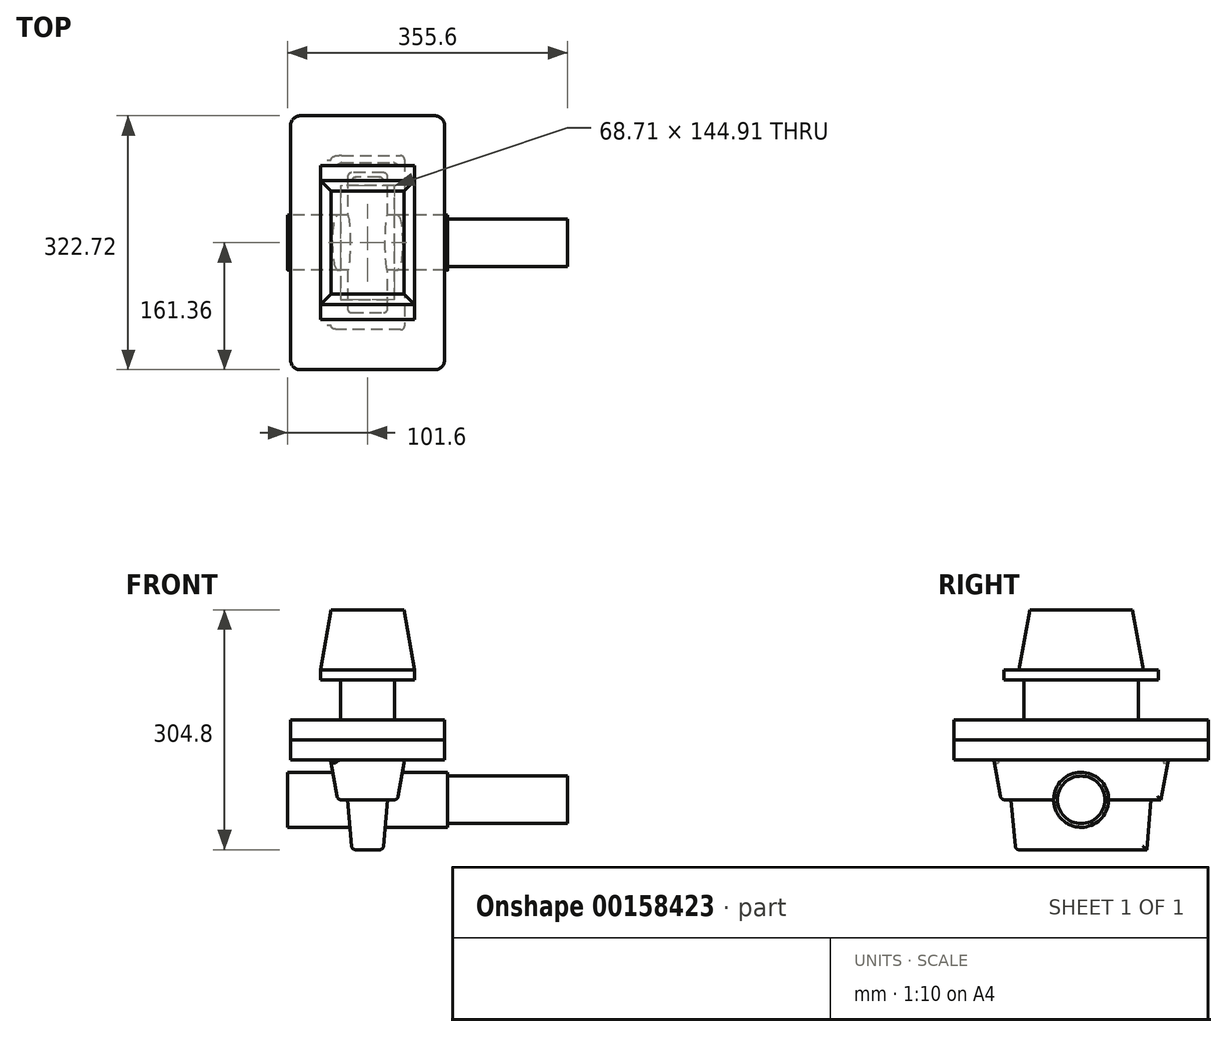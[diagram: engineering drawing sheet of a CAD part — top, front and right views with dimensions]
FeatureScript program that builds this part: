
annotation { "Feature Type Name" : "Feature", "Feature Type Description" : "" }
export const myFeature = defineFeature(function(context is Context, id is Id, definition is map)
    precondition{}
    {
        {
            var Q0;
            Q0=qCreatedBy(makeId("Top.planeOp"),FACE);
            var sketch = newSketch(context, id + "F0", { "sketchPlane" : qUnion([Q0])});
            skLineSegment(sketch, "E0.bottom", {"start": v(-38.1, -101.6) * mm, "end": v(38.1, -101.6) * mm});
            skLineSegment(sketch, "E0.top", {"start": v(-38.1, 101.6) * mm, "end": v(38.1, 101.6) * mm});
            skLineSegment(sketch, "E0.left", {"start": v(-38.1, -101.6) * mm, "end": v(-38.1, 101.6) * mm});
            skLineSegment(sketch, "E0.right", {"start": v(38.1, -101.6) * mm, "end": v(38.1, 101.6) * mm});
            skSolve(sketch);
        }
        {
            var Q0;
            Q0=makeQuery(id+"F0.imprint","IMPRINT",FACE,{"disambiguationData":[TD([[makeQuery(id+"F0.imprint","IMPRINT",EDGE,{"derivedFrom":sQuery(id+"F0.wireOp",EDGE,"E0.bottom")}),1.0]])]});
            extrude(context, id + "F1", {"entities" : qUnion([Q0]), "depth" : 50.8 * mm, "hasDraft" : true, "draftAngle" : 10 * degree});
        }
        {
            var Q0;
            Q0=makeQuery(id+"F1.opExtrude","CAP_FACE",FACE,{"disambiguationData":[OSD([sQuery(id+"F0.wireOp",EDGE,"E0.bottom"),sQuery(id+"F0.wireOp",EDGE,"E0.top"),sQuery(id+"F0.wireOp",EDGE,"E0.left"),sQuery(id+"F0.wireOp",EDGE,"E0.right")])],"isStart":false});
            var sketch = newSketch(context, id + "F2", { "sketchPlane" : qUnion([Q0])});
            skLineSegment(sketch, "E1.0", {"start": v(97.86, 161.36) * mm, "end": v(-97.86, 161.36) * mm});
            skLineSegment(sketch, "E1.1", {"start": v(97.86, -161.36) * mm, "end": v(97.86, 161.36) * mm});
            skLineSegment(sketch, "E1.2", {"start": v(-97.86, -161.36) * mm, "end": v(97.86, -161.36) * mm});
            skLineSegment(sketch, "E1.3", {"start": v(-97.86, 161.36) * mm, "end": v(-97.86, -161.36) * mm});
            skSolve(sketch);
        }
        {
            var Q0;
            Q0=makeQuery(id+"F2.imprint","IMPRINT",FACE,{"disambiguationData":[TD([[makeQuery(id+"F2.imprint","IMPRINT",EDGE,{"derivedFrom":sQuery(id+"F2.wireOp",EDGE,"E1.0")}),1.0]])]});
            var Q1;
            Q1=makeQuery(id+"F2.imprint","IMPRINT",FACE,{"disambiguationData":[TD([[makeQuery(id+"F2.imprint","IMPRINT",EDGE,{"derivedFrom":makeQuery(id+"F1.opExtrude","CAP_EDGE",EDGE,{"disambiguationData":[OSD([sQuery(id+"F0.wireOp",EDGE,"E0.bottom")])],"isStart":false})}),1.0]])]});
            extrude(context, id + "F3", {"entities" : qUnion([Q0, Q1]), "operationType" : NewBodyOperationType.ADD, "depth" : 25.4 * mm});
        }
        {
            var Q0;
            Q0=makeQuery(id+"F3.opExtrude","CAP_FACE",FACE,{"disambiguationData":[OSD([sQuery(id+"F2.wireOp",EDGE,"E1.0"),sQuery(id+"F2.wireOp",EDGE,"E1.1"),sQuery(id+"F2.wireOp",EDGE,"E1.2"),sQuery(id+"F2.wireOp",EDGE,"E1.3")])],"isStart":false});
            extrude(context, id + "F4", {"entities" : qUnion([Q0]), "depth" : 25.4 * mm});
        }
        {
            var Q0;
            Q0=makeQuery(id+"F4.opExtrude","SWEPT_EDGE",EDGE,{"disambiguationData":[OSD([sQuery(id+"F2.wireOp",EDGE,"E1.2"),sQuery(id+"F2.wireOp",EDGE,"E1.3")])]});
            var Q1;
            Q1=makeQuery(id+"F4.opExtrude","SWEPT_EDGE",EDGE,{"disambiguationData":[OSD([sQuery(id+"F2.wireOp",EDGE,"E1.1"),sQuery(id+"F2.wireOp",EDGE,"E1.2")])]});
            var Q2;
            Q2=makeQuery(id+"F3.opExtrude","SWEPT_EDGE",EDGE,{"disambiguationData":[OSD([sQuery(id+"F2.wireOp",EDGE,"E1.1"),sQuery(id+"F2.wireOp",EDGE,"E1.2")])]});
            var Q3;
            Q3=makeQuery(id+"F3.opExtrude","SWEPT_EDGE",EDGE,{"disambiguationData":[OSD([sQuery(id+"F2.wireOp",EDGE,"E1.2"),sQuery(id+"F2.wireOp",EDGE,"E1.3")])]});
            var Q4;
            Q4=makeQuery(id+"F3.opExtrude","SWEPT_EDGE",EDGE,{"disambiguationData":[OSD([sQuery(id+"F2.wireOp",EDGE,"E1.0"),sQuery(id+"F2.wireOp",EDGE,"E1.1")])]});
            var Q5;
            Q5=makeQuery(id+"F4.opExtrude","SWEPT_EDGE",EDGE,{"disambiguationData":[OSD([sQuery(id+"F2.wireOp",EDGE,"E1.0"),sQuery(id+"F2.wireOp",EDGE,"E1.1")])]});
            var Q6;
            Q6=makeQuery(id+"F3.opExtrude","SWEPT_EDGE",EDGE,{"disambiguationData":[OSD([sQuery(id+"F2.wireOp",EDGE,"E1.0"),sQuery(id+"F2.wireOp",EDGE,"E1.3")])]});
            var Q7;
            Q7=makeQuery(id+"F4.opExtrude","SWEPT_EDGE",EDGE,{"disambiguationData":[OSD([sQuery(id+"F2.wireOp",EDGE,"E1.0"),sQuery(id+"F2.wireOp",EDGE,"E1.3")])]});
            fillet(context, id + "F5", {"entities" : qUnion([Q0, Q1, Q2, Q3, Q4, Q5, Q6, Q7]), "radius" : 12.7 * mm, "tangentPropagation" : true, "allowEdgeOverflow" : false});
        }
        {
            var Q0;
            Q0=makeQuery(id+"F1.opExtrude","CAP_FACE",FACE,{"disambiguationData":[OSD([sQuery(id+"F0.wireOp",EDGE,"E0.bottom"),sQuery(id+"F0.wireOp",EDGE,"E0.top"),sQuery(id+"F0.wireOp",EDGE,"E0.left"),sQuery(id+"F0.wireOp",EDGE,"E0.right")])],"isStart":true});
            var sketch = newSketch(context, id + "F6", { "sketchPlane" : qUnion([Q0])});
            skLineSegment(sketch, "E2.0", {"start": v(-25.4, -88.9) * mm, "end": v(25.4, -88.9) * mm});
            skLineSegment(sketch, "E2.1", {"start": v(-25.4, 88.9) * mm, "end": v(-25.4, -88.9) * mm});
            skLineSegment(sketch, "E2.2", {"start": v(-25.4, 88.9) * mm, "end": v(25.4, 88.9) * mm});
            skLineSegment(sketch, "E2.3", {"start": v(25.4, 88.9) * mm, "end": v(25.4, -88.9) * mm});
            skSolve(sketch);
        }
        {
            var Q0;
            Q0=makeQuery(id+"F6.imprint","IMPRINT",FACE,{"disambiguationData":[TD([[makeQuery(id+"F6.imprint","IMPRINT",EDGE,{"derivedFrom":sQuery(id+"F6.wireOp",EDGE,"E2.0")}),1.0]])]});
            extrude(context, id + "F7", {"entities" : qUnion([Q0]), "operationType" : NewBodyOperationType.ADD, "depth" : 63.5 * mm, "hasDraft" : true, "draftAngle" : 5 * degree, "draftPullDirection" : true});
        }
        {
            var Q0;
            Q0=makeQuery(id+"F1.opExtrude","CAP_EDGE",EDGE,{"disambiguationData":[OSD([sQuery(id+"F0.wireOp",EDGE,"E0.right")])],"isStart":true});
            var Q1;
            Q1=makeQuery(id+"F7.opExtrude","CAP_EDGE",EDGE,{"disambiguationData":[OSD([sQuery(id+"F6.wireOp",EDGE,"E2.3")])],"isStart":false});
            var Q2;
            Q2=makeQuery(id+"F7.opExtrude","SWEPT_EDGE",EDGE,{"disambiguationData":[OSD([sQuery(id+"F6.wireOp",EDGE,"E2.2"),sQuery(id+"F6.wireOp",EDGE,"E2.3")])]});
            var Q3;
            Q3=makeQuery(id+"F7.opExtrude","SWEPT_EDGE",EDGE,{"disambiguationData":[OSD([sQuery(id+"F6.wireOp",EDGE,"E2.0"),sQuery(id+"F6.wireOp",EDGE,"E2.3")])]});
            var Q4;
            Q4=makeQuery(id+"F1.opExtrude","SWEPT_EDGE",EDGE,{"disambiguationData":[OSD([sQuery(id+"F0.wireOp",EDGE,"E0.top"),sQuery(id+"F0.wireOp",EDGE,"E0.right")])]});
            var Q5;
            Q5=makeQuery(id+"F1.opExtrude","SWEPT_EDGE",EDGE,{"disambiguationData":[OSD([sQuery(id+"F0.wireOp",EDGE,"E0.bottom"),sQuery(id+"F0.wireOp",EDGE,"E0.right")])]});
            var Q6;
            Q6=makeQuery(id+"F1.opExtrude","CAP_EDGE",EDGE,{"disambiguationData":[OSD([sQuery(id+"F0.wireOp",EDGE,"E0.bottom")])],"isStart":true});
            var Q7;
            Q7=makeQuery(id+"F1.opExtrude","SWEPT_EDGE",EDGE,{"disambiguationData":[OSD([sQuery(id+"F0.wireOp",EDGE,"E0.bottom"),sQuery(id+"F0.wireOp",EDGE,"E0.left")])]});
            var Q8;
            Q8=makeQuery(id+"F7.opExtrude","SWEPT_EDGE",EDGE,{"disambiguationData":[OSD([sQuery(id+"F6.wireOp",EDGE,"E2.1"),sQuery(id+"F6.wireOp",EDGE,"E2.2")])]});
            var Q9;
            Q9=makeQuery(id+"F7.opExtrude","CAP_EDGE",EDGE,{"disambiguationData":[OSD([sQuery(id+"F6.wireOp",EDGE,"E2.2")])],"isStart":false});
            var Q10;
            Q10=makeQuery(id+"F7.opExtrude","CAP_EDGE",EDGE,{"disambiguationData":[OSD([sQuery(id+"F6.wireOp",EDGE,"E2.1")])],"isStart":false});
            var Q11;
            Q11=makeQuery(id+"F7.opExtrude","SWEPT_EDGE",EDGE,{"disambiguationData":[OSD([sQuery(id+"F6.wireOp",EDGE,"E2.0"),sQuery(id+"F6.wireOp",EDGE,"E2.1")])]});
            var Q12;
            Q12=makeQuery(id+"F1.opExtrude","SWEPT_FACE",FACE,{"disambiguationData":[OSD([sQuery(id+"F0.wireOp",EDGE,"E0.left")])]});
            fillet(context, id + "F8", {"entities" : qUnion([Q0, Q1, Q2, Q3, Q4, Q5, Q6, Q7, Q8, Q9, Q10, Q11, Q12]), "radius" : 5.08 * mm, "tangentPropagation" : true, "allowEdgeOverflow" : false});
        }
        {
            var Q0;
            Q0=makeQuery(id+"F4.opExtrude","CAP_FACE",FACE,{"disambiguationData":[OSD([sQuery(id+"F2.wireOp",EDGE,"E1.0"),sQuery(id+"F2.wireOp",EDGE,"E1.1"),sQuery(id+"F2.wireOp",EDGE,"E1.2"),sQuery(id+"F2.wireOp",EDGE,"E1.3")])],"isStart":false});
            var sketch = newSketch(context, id + "F9", { "sketchPlane" : qUnion([Q0])});
            skLineSegment(sketch, "E3.0", {"start": v(34.36, -72.46) * mm, "end": v(34.36, 72.46) * mm});
            skLineSegment(sketch, "E4.0", {"start": v(-34.36, 72.46) * mm, "end": v(-34.36, -72.46) * mm});
            skLineSegment(sketch, "E5.0", {"start": v(-34.36, -72.46) * mm, "end": v(34.36, -72.46) * mm});
            skLineSegment(sketch, "E6.0", {"start": v(34.36, 72.46) * mm, "end": v(-34.36, 72.46) * mm});
            skSolve(sketch);
        }
        {
            var Q0;
            Q0=makeQuery(id+"F9.imprint","IMPRINT",FACE,{"disambiguationData":[TD([[makeQuery(id+"F9.imprint","IMPRINT",EDGE,{"derivedFrom":sQuery(id+"F9.wireOp",EDGE,"E3.0")}),1.0]])]});
            extrude(context, id + "F10", {"entities" : qUnion([Q0]), "operationType" : NewBodyOperationType.ADD, "depth" : 50.8 * mm});
        }
        {
            var Q0;
            Q0=makeQuery(id+"F10.opExtrude","CAP_FACE",FACE,{"disambiguationData":[OSD([sQuery(id+"F9.wireOp",EDGE,"E3.0"),sQuery(id+"F9.wireOp",EDGE,"E4.0"),sQuery(id+"F9.wireOp",EDGE,"E5.0"),sQuery(id+"F9.wireOp",EDGE,"E6.0")])],"isStart":false});
            var sketch = newSketch(context, id + "F11", { "sketchPlane" : qUnion([Q0])});
            skLineSegment(sketch, "E7.0", {"start": v(59.76, 97.86) * mm, "end": v(-59.76, 97.86) * mm});
            skLineSegment(sketch, "E7.1", {"start": v(59.76, -97.86) * mm, "end": v(59.76, 97.86) * mm});
            skLineSegment(sketch, "E7.2", {"start": v(-59.76, -97.86) * mm, "end": v(59.76, -97.86) * mm});
            skLineSegment(sketch, "E7.3", {"start": v(-59.76, 97.86) * mm, "end": v(-59.76, -97.86) * mm});
            skSolve(sketch);
        }
        {
            var Q0;
            Q0=makeQuery(id+"F11.imprint","IMPRINT",FACE,{"disambiguationData":[TD([[makeQuery(id+"F11.imprint","IMPRINT",EDGE,{"derivedFrom":sQuery(id+"F11.wireOp",EDGE,"E7.0")}),1.0]])]});
            var Q1;
            Q1=makeQuery(id+"F11.imprint","IMPRINT",FACE,{"disambiguationData":[TD([[makeQuery(id+"F11.imprint","IMPRINT",EDGE,{"derivedFrom":makeQuery(id+"F10.opExtrude","CAP_EDGE",EDGE,{"disambiguationData":[OSD([sQuery(id+"F9.wireOp",EDGE,"E3.0")])],"isStart":false})}),1.0]])]});
            extrude(context, id + "F12", {"entities" : qUnion([Q0, Q1]), "operationType" : NewBodyOperationType.ADD, "depth" : 12.7 * mm});
        }
        {
            var Q0;
            Q0=makeQuery(id+"F12.opExtrude","CAP_FACE",FACE,{"disambiguationData":[OSD([sQuery(id+"F11.wireOp",EDGE,"E7.0"),sQuery(id+"F11.wireOp",EDGE,"E7.1"),sQuery(id+"F11.wireOp",EDGE,"E7.2"),sQuery(id+"F11.wireOp",EDGE,"E7.3")])],"isStart":false});
            var sketch = newSketch(context, id + "F13", { "sketchPlane" : qUnion([Q0])});
            skLineSegment(sketch, "E8.0", {"start": v(-59.76, -78.8) * mm, "end": v(59.76, -78.8) * mm});
            skLineSegment(sketch, "E9.0", {"start": v(59.76, 78.8) * mm, "end": v(-59.76, 78.8) * mm});
            skSolve(sketch);
        }
        {
            var Q0;
            {var subQ0=sQuery(id+"F13.wireOp",EDGE,"E8.0");Q0=makeQuery(id+"F13.imprint","IMPRINT",FACE,{"disambiguationData":[TD([[makeQuery(id+"F13.imprint","IMPRINT",EDGE,{"derivedFrom":subQ0}),1.0]])]});}
            extrude(context, id + "F14", {"entities" : qUnion([Q0]), "operationType" : NewBodyOperationType.ADD, "depth" : 76.2 * mm, "hasDraft" : true, "draftAngle" : 10 * degree, "draftPullDirection" : true});
        }
        {
            var Q0;
            Q0=qCreatedBy(makeId("Right.planeOp"),FACE);
            var sketch = newSketch(context, id + "F15", { "sketchPlane" : qUnion([Q0])});
            skCircle(sketch, "E10", {"center": v(0, 0) * mm, "radius": 34.93 * mm});
            skSolve(sketch);
        }
        {
            var Q0;
            Q0 = qSketchRegion(id + "F15", true);
            extrude(context, id + "F16", {"entities" : qUnion([Q0]), "operationType" : NewBodyOperationType.ADD, "depth" : 101.6 * mm, "hasSecondDirection" : true, "secondDirectionOppositeDirection" : true, "secondDirectionDepth" : 101.6 * mm});
        }
        {
            var Q0;
            Q0=makeQuery(id+"F16.opExtrude","CAP_FACE",FACE,{"disambiguationData":[OSD([sQuery(id+"F15.wireOp",EDGE,"E10")])],"isStart":false});
            var sketch = newSketch(context, id + "F17", { "sketchPlane" : qUnion([Q0])});
            skCircle(sketch, "E11.0", {"center": v(0, 0) * mm, "radius": 30.16 * mm});
            skSolve(sketch);
        }
        {
            var Q0;
            Q0=makeQuery(id+"F17.imprint","IMPRINT",FACE,{"disambiguationData":[TD([[makeQuery(id+"F17.imprint","IMPRINT",EDGE,{"derivedFrom":sQuery(id+"F17.wireOp",EDGE,"E11.0")}),1.0]])]});
            extrude(context, id + "F18", {"entities" : qUnion([Q0]), "operationType" : NewBodyOperationType.ADD, "depth" : 152.4 * mm});
        }
    });
